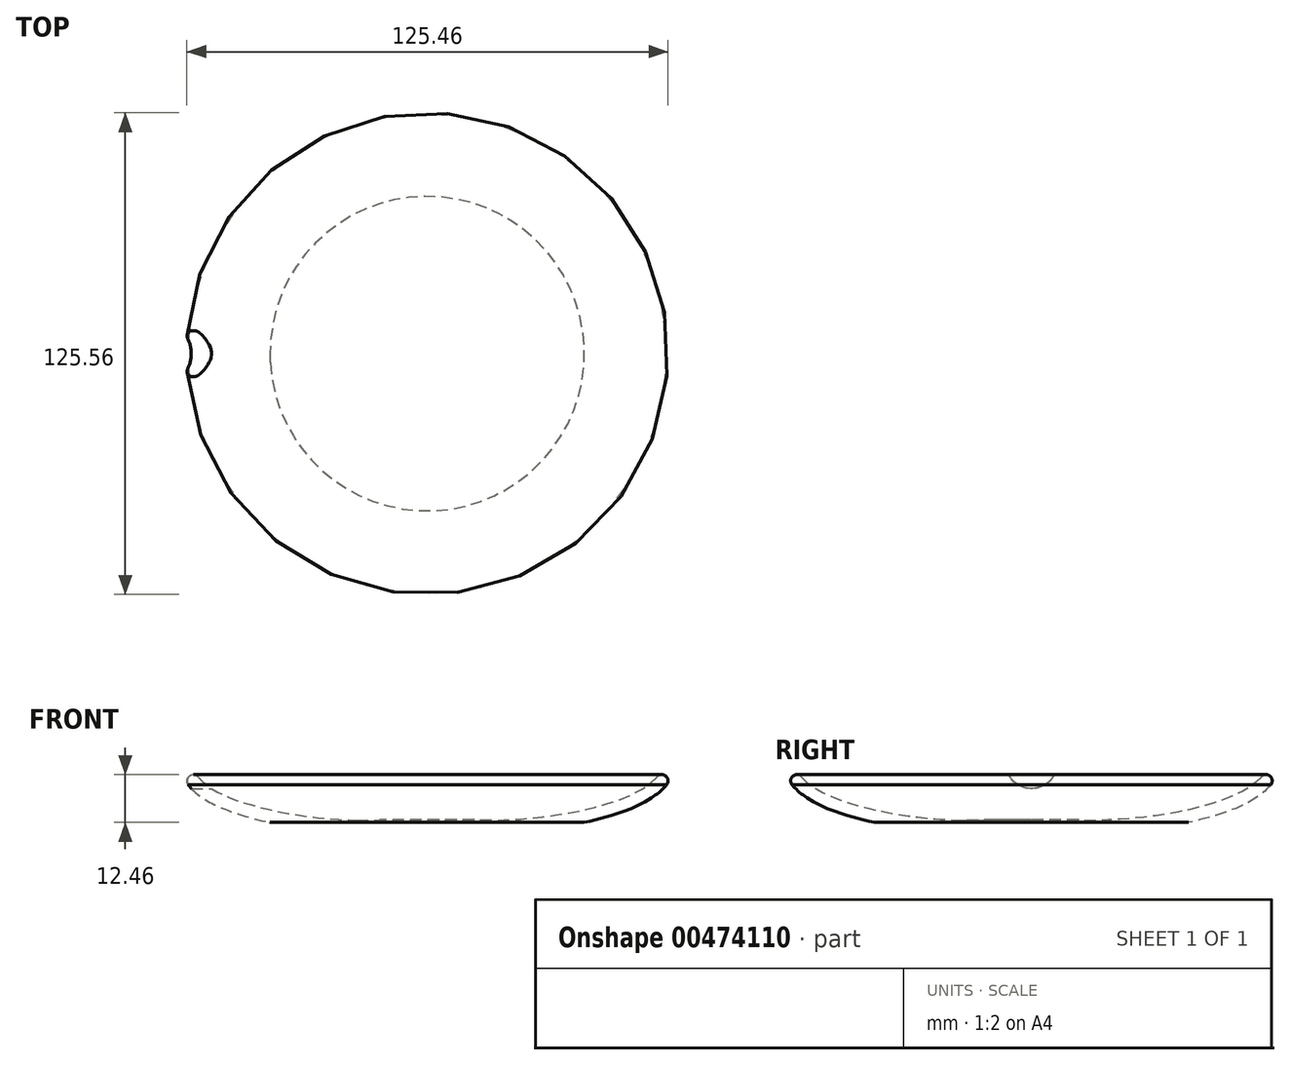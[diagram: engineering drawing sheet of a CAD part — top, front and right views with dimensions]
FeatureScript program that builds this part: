
annotation { "Feature Type Name" : "Feature", "Feature Type Description" : "" }
export const myFeature = defineFeature(function(context is Context, id is Id, definition is map)
    precondition{}
    {
        {
            var Q0;
            Q0=qCreatedBy(makeId("Front.planeOp"),FACE);
            var sketch = newSketch(context, id + "F0", { "sketchPlane" : qUnion([Q0])});
            skLineSegment(sketch, "E0", {"start": v(0, 0) * mm, "end": v(0, 3.18) * mm});
            skFitSpline(sketch, "E1", {"points": [v(0, 3.18) * mm, v(15.67, 3.18) * mm, v(20.41, 3.18) * mm, v(40.43, 5.72) * mm, v(59.98, 14.43) * mm], "startDerivative": vector(102.02, 0) * mm, "endDerivative": vector(33.66, 40.49) * mm});
            skFitSpline(sketch, "E2.0", {"points": [v(0, 0) * mm, v(2.13, 0) * mm, v(5.83, 0) * mm, v(10, 0.02) * mm, v(12.59, 0.02) * mm, v(14.25, 0.02) * mm, v(15.34, 0) * mm, v(16.3, -0.01) * mm, v(17.23, -0.03) * mm, v(18.23, -0.04) * mm, v(19.36, -0.03) * mm, v(20.67, 0) * mm, v(22.22, 0.08) * mm, v(23.99, 0.2) * mm, v(26.6, 0.4) * mm, v(30.3, 0.78) * mm, v(35.18, 1.47) * mm, v(40.33, 2.4) * mm, v(45.53, 3.63) * mm, v(50.55, 5.17) * mm, v(55.2, 7.06) * mm, v(58.6, 8.97) * mm, v(60.93, 10.8) * mm, v(61.95, 11.84) * mm, v(62.42, 12.4) * mm]});
            skArc(sketch, "E3", {"start": v(62.42, 12.4) * mm, "mid": v(62.21, 14.63) * mm, "end": v(59.98, 14.43) * mm});
            skSolve(sketch);
        }
        {
            var Q0;
            Q0 = qSketchRegion(id + "F0", true);
            var Q1;
            Q1=sQuery(id+"F0.wireOp",EDGE,"E0");
            revolve(context, id + "F1", {"entities" : qUnion([Q0]), "axis" : qUnion([Q1]), "revolveType" : RevolveType.FULL});
        }
        {
            var Q0;
            Q0=qCreatedBy(makeId("Top.planeOp"),FACE);
            var sketch = newSketch(context, id + "F2", { "sketchPlane" : qUnion([Q0])});
            skCircle(sketch, "E4", {"center": v(0, 0) * mm, "radius": 90.38 * mm});
            skSolve(sketch);
        }
        {
            var Q0;
            Q0 = qSketchRegion(id + "F2", true);
            extrude(context, id + "F3", {"entities" : qUnion([Q0]), "operationType" : NewBodyOperationType.REMOVE, "endBound" : BoundingType.SYMMETRIC, "depth" : 5.08 * mm});
        }
        {
            var Q0;
            Q0=qCreatedBy(makeId("Right.planeOp"),FACE);
            var sketch = newSketch(context, id + "F4", { "sketchPlane" : qUnion([Q0])});
            skCircle(sketch, "E5", {"center": v(0, 18.11) * mm, "radius": 6.76 * mm});
            skLineSegment(sketch, "E6", {"start": v(0, 18.11) * mm, "end": v(0, 39.42) * mm, "construction": true});
            skSolve(sketch);
        }
        {
            var Q0;
            Q0 = qSketchRegion(id + "F4", true);
            extrude(context, id + "F5", {"entities" : qUnion([Q0]), "operationType" : NewBodyOperationType.REMOVE, "oppositeDirection" : true, "depth" : 68.33 * mm});
        }
    });
